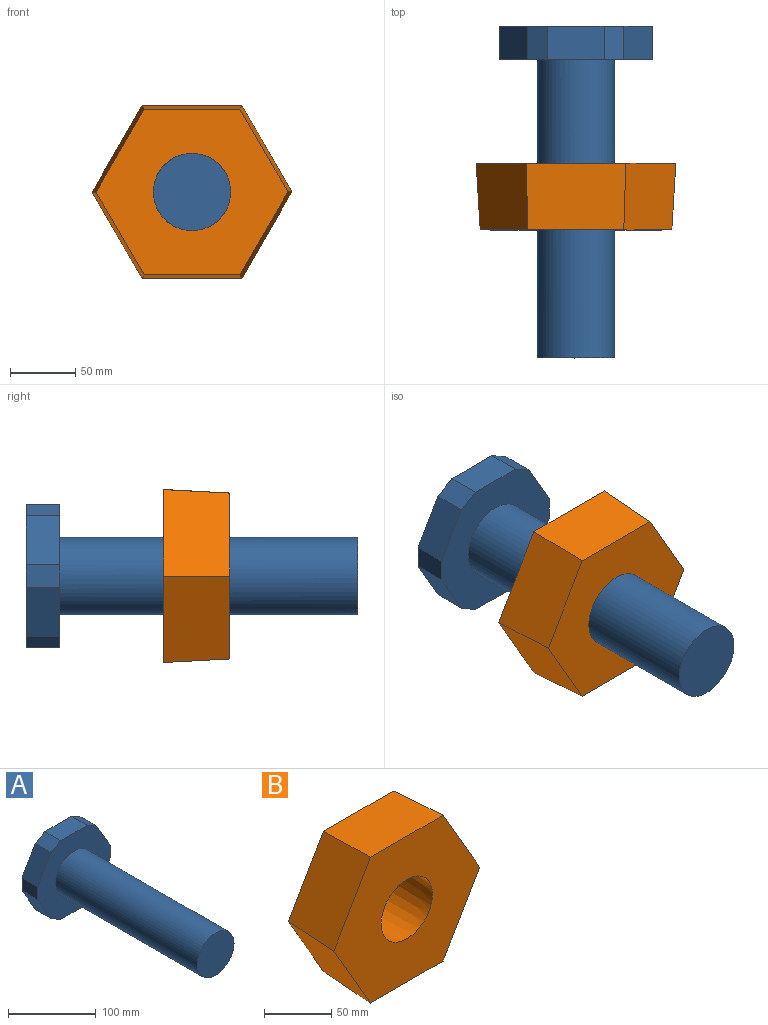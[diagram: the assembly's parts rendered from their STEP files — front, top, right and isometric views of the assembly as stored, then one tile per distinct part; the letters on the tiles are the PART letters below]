
ASSEMBLY  parts=2 mates=1
PART A: 16 faces, bbox 116.9x254x110.1 mm
  f0: plane 37.34x25.4mm, normal (-0.86,0,-0.5), area 1096.8mm2, adj f6,f7,f14,f15
  f1: plane 43.18x25.4mm, normal (0,0,-1), area 1096.8mm2, adj f6,f7,f13,f14
  f2: plane 37.45x25.4mm, normal (0.87,0,-0.5), area 1096.8mm2, adj f6,f7,f12,f13
  f3: plane 37.34x25.4mm, normal (0.86,0,0.5), area 1096.8mm2, adj f6,f7,f11,f12
  f4: plane 43.18x25.4mm, normal (0,0,1), area 1096.8mm2, adj f6,f7,f10,f11
  f5: plane 37.45x25.4mm, normal (-0.87,0,0.5), area 1096.8mm2, adj f6,f7,f10,f15
  f6: plane 116.88x110.09mm, normal (0,-1,0), area 7456.8mm2, adj f0,f1,f2,f3,f4,f5,f8,f10
  f7: plane 116.88x110.09mm, normal (0,1,0), area 10208mm2, adj f0,f1,f2,f3,f4,f5,f10,f11
  f8: cylinder r=29.59mm len=228.6mm, axis (0,1,0), area 42505.2mm2, adj f6,f9
  f9: plane 59.19x59.19mm, normal (0,-1,0), area 2751.2mm2, adj f8
  f10: plane 25.4x15.22mm, normal (-0.5,0,0.86), area 447mm2, adj f4,f5,f6,f7
  f11: plane 25.4x15.26mm, normal (0.5,0,0.87), area 447mm2, adj f3,f4,f6,f7
  f12: plane 25.4x17.6mm, normal (1,0,0), area 447mm2, adj f2,f3,f6,f7
  f13: plane 25.4x15.22mm, normal (0.5,0,-0.86), area 447mm2, adj f1,f2,f6,f7
  f14: plane 25.4x15.26mm, normal (-0.5,0,-0.87), area 447mm2, adj f0,f1,f6,f7
  f15: plane 25.4x17.6mm, normal (-1,0,0), area 447mm2, adj f0,f5,f6,f7
PART B: 9 faces, bbox 152.8x50.8x132.4 mm
  f0: plane 66.2x50.8mm, normal (-0.87,0.05,-0.5), area 3808.1mm2, adj f1,f6,f7,f8
  f1: plane 76.4x50.8mm, normal (0,0.05,-1), area 3808.1mm2, adj f0,f2,f7,f8
  f2: plane 66.13x50.8mm, normal (0.86,0.05,-0.5), area 3808.1mm2, adj f1,f3,f7,f8
  f3: plane 66.2x50.8mm, normal (0.87,0.05,0.5), area 3808.1mm2, adj f2,f4,f7,f8
  f4: plane 76.4x50.8mm, normal (0,0.05,1), area 3808.1mm2, adj f3,f6,f7,f8
  f5: cone r=29.59mm half-angle=3deg, axis (0,1,0), area 9032.5mm2, adj f7,f8
  f6: plane 66.13x50.8mm, normal (-0.86,0.05,0.5), area 3808.1mm2, adj f0,f4,f7,f8
  f7: plane 152.8x132.4mm, normal (0,-1,0), area 12885.8mm2, adj f0,f1,f2,f3,f4,f5,f6
  f8: plane 146.65x127.07mm, normal (0,1,0), area 11217.3mm2, adj f0,f1,f2,f3,f4,f5,f6
PLACE A t=(-62.98,98.18,-21.42)mm
PLACE B rot(axis=(1,0,0),180deg) t=(-62.98,-57.87,-21.42)mm
MATE cylindrical B.f5 <-> A.f8  axis (0,-1,0) through (-62.98,-7.07,-21.42)mm
